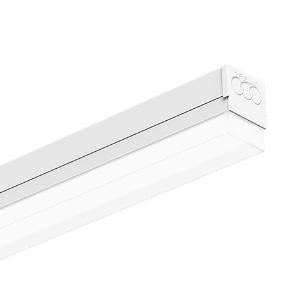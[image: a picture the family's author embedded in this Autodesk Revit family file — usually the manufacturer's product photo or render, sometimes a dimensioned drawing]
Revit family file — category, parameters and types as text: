
# Revit family: 3f_filippi_-_3f_zeta_dr_3f_filippi_-_10878_-_3f_zeta_dr_1x18_led_l1194
name_source: partatom
category: Lighting Fixtures
units: mm (PartAtom-declared; Revit-internal decimal feet)

## family parameters
Cut with Voids When Loaded = No
Host = Face
Light Source = No
Part Type = Normal
Room Calculation Point = No
Round Connector Dimension = Use Diameter
Shared = No

## types (1)
- 3F Filippi - 3F Zeta DR (1 x LED, 2425 lm, 20 W, 4000 K)
    Apparent Load = 20 VA
    Approval mark = CE
    CIE Flux Codes = 41 72 91 86 100
    Color Rendering = 80
    Color Temperature = 4000 K
    Control Gear = Electronic ballast
    Default Elevation = 1800 mm
    Description = ILLUMINOTECHNICAL
Luminous efficiency 100% (DLOR 86%, ULOR 14%).
Initial luminous flux of the luminaire 2425 lm.
Diffused symmetric distribution.
Installation Interdistance Transv.D = 1.31 x hu - Long.D = 1.25 x hu.
Tabular UGR (CIE 117 - 4H-8H; S=0.25H; 70/50/20): RUG 23.1 - 21.7.
Beam angle: 136° - 112°.
Luminous efficacy 121 lm/W.
Lifetime (L93/B10): 30000 h. (tq+25°C)
Lifetime (L90/B10): 50000 h. (tq+25°C)
Lifetime (L85/B10): 80000 h. (tq+25°C)
Lifetime (L80/B10): 100000 h. (tq+25°C)
Sudden decreased luminous flux after 50000 hours: 0% (C0).
Photobiological safety in compliance with IEC/TR 62778: RG0 risk exempt, (IEC 62471).
In compliance with IEC/EN 62722-2-1 - IEC/EN 62717 standards.

SOURCE
Linear LED module 18W/840.
Energy efficiency class (UE 2019/2020 - UE 2019/2015): D.
CIE 13.3 Colour rendering index: CRI >80 (R9 <50%).
IES TM-30 Fidelity Index: Rf = 84 Rg = 95.
CCT nominal colour temperature 4000 K.
Colour initial tolerance (MacAdam): SDCM 3.

MECHANICAL
Housing in hot-galvanised steel, painted in white polyester, obtained through rolling process.
Light unit in hot-galvanised steel, painted in white polyester base with fixing springs and retractable safety hooks in stainless steel.
Rectangular screen in self-extinguishing polycarbonate, UV stabilised, opal, with smooth outer surface.
End caps in white polycarbonate.
Pair of stainless steel sliding brackets with sliding block screws.
Luminaire with limited surface temperature. - D - (EN 60598-2-24)
Dimensions: 1194x62 mm, height 81 mm. Weight 2.855 kg.
IP40 protection degree.
Mechanical strength to impacts IK06 (1 joule).
Glow-wire test resistance 850°C.

ELECTRICAL
Halogen Free electronic wiring 230V-50/60Hz, power factor 0.90, THD <25%, constant output current, SELV, class I, 1 driver.
Power of the luminaire 20 W.
ENEC - CE.
SAFE FLICKER: PstLM=<1 and SVM=<0.4 (IEC TR 61547-1 and IEC TR 63158), to ensure a more comfortable and safe light.
Luminaire compliant with EN 60598-2-22 for power supply from a centralised emergency system CPSS (Central Power Supply System), not incorporated in the luminaire - high risk areas excluded. The default power and flux are 100% in AC and 100% in DC.
Ambient temperature from 0°C to +25°C.
Temperature class T6 max 85°C.
Relative humidity UR: <85%.

INSTALLATION
Ceiling / Suspended / Wall.
All accessories dedicated to this product are available on the Catalog and on our website www.3F-Filippi.com.

APPLICATIONS
Suitable product for food production plants (HACCP), IFS (Food Version 6), BRC (GSFS Food Version 7).
In commercial environments, exhibition areas, shops and stores.

WARNING
Luminaire designed for disposal/recycling at end-of-life.
Replaceable (LED only) light source by a professional. Replaceable control gear by a professional.
    Height = 81 mm
    Lamp = 1 x LED
    Lamp Light Flux = 2425 lm
    Lamp Power = 20 W
    Lamp count = 1
    Length = 1194 mm
    Lifetime = 50000 h
    Luminous efficacy = 121 lm/W
    Manufacturer = 3F Filippi
    ModVariant = No
    Model = 3F Filippi - 10878 - 3F Zeta DR 1x18 LED L1194
    Mounting Place = Ceiling
    Mounting Type = Pendant
    Number of Poles = 1
    OnlyDefault = Yes
    Power Factor = 1
    Product Name = 3F Filippi - 3F Zeta DR
    Product group = pendant luminaire
    ProductGroupID = 9
    Protection Class = Protection class I
    Protection Degree = IP 40
    RLX_Detail_Level = 1
    RLX_Emergency_Light_Flux = 0 lm
    RLX_Emergency_Type = 0
    RLX_Emergency_Type_DB = No
    RlxData = <blob elided: 33057 chars, md5=5cc08869>
    Socket = socket
    Standby Power = 0 W
    System Light Flux = 2425 lm
    System Power = 20 W
    Type Comments = Product without accessories
    Type Image = 3ffilippi_3f_zeta_dr.jpg
    URL = http://relux.com
    VarID = ---
    Voltage = 0 V
    Weight = 0.00 kg
    Width = 62 mm  [stored 0.203412 ft]

note: [stored X ft] marks values corroborated as IEEE doubles in the binary element streams (Revit-internal decimal feet)

## geometry (parser evidence)
native form markers: Blend x4, Sweep x14
no freeform markers — native parametric forms only
